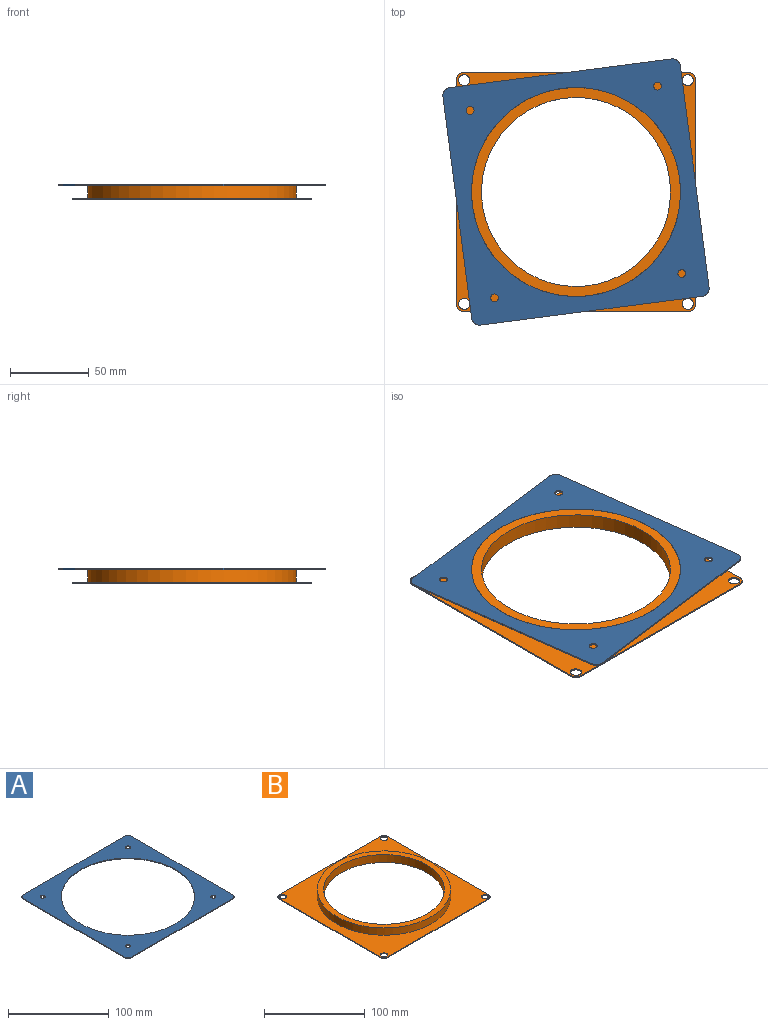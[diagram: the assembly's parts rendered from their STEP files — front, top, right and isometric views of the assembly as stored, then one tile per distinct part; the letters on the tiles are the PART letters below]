
ASSEMBLY  parts=2 mates=1
PART A: 15 faces, bbox 152x152x0.8 mm
  f0: cylinder r=5mm len=5mm, axis (0,0,1), area 6.3mm2, adj f1,f12,f13,f14
  f1: plane 142x0.8mm, normal (0,-1,0), area 113.6mm2, adj f0,f2,f13,f14
  f2: cylinder r=5mm len=5mm, axis (0,0,1), area 6.3mm2, adj f1,f3,f13,f14
  f3: plane 142x0.8mm, normal (1,0,0), area 113.6mm2, adj f2,f4,f13,f14
  f4: cylinder r=5mm len=5mm, axis (0,0,1), area 6.3mm2, adj f3,f5,f13,f14
  f5: plane 142x0.8mm, normal (0,1,0), area 113.6mm2, adj f4,f6,f13,f14
  f6: cylinder r=5mm len=5mm, axis (0,0,1), area 6.3mm2, adj f5,f12,f13,f14
  f7: cylinder r=2.5mm len=5mm, axis (0,0,1), area 12.6mm2, adj f13,f14
  f8: cylinder r=2.5mm len=5mm, axis (0,0,1), area 12.6mm2, adj f13,f14
  f9: cylinder r=2.5mm len=5mm, axis (0,0,1), area 12.6mm2, adj f13,f14
  f10: cylinder r=2.5mm len=5mm, axis (0,0,1), area 12.6mm2, adj f13,f14
  f11: cylinder r=66.35mm len=132.7mm, axis (0,0,1), area 333.5mm2, adj f13,f14
  f12: plane 142x0.8mm, normal (-1,0,0), area 113.6mm2, adj f0,f6,f13,f14
  f13: plane 152x152mm, normal (0,0,-1), area 9173.7mm2, adj f0,f1,f2,f3,f4,f5,f6,f7
  f14: plane 152x152mm, normal (0,0,1), area 9173.7mm2, adj f0,f1,f2,f3,f4,f5,f6,f7
PART B: 17 faces, bbox 152x152x9.6 mm
  f0: plane 142x0.8mm, normal (0,-1,0), area 113.6mm2, adj f1,f12,f13,f14
  f1: cylinder r=5mm len=5mm, axis (0,0,-1), area 6.3mm2, adj f0,f2,f13,f14
  f2: plane 142x0.8mm, normal (1,0,0), area 113.6mm2, adj f1,f3,f13,f14
  f3: cylinder r=5mm len=5mm, axis (0,0,-1), area 6.3mm2, adj f2,f4,f13,f14
  f4: plane 142x0.8mm, normal (0,1,0), area 113.6mm2, adj f3,f5,f13,f14
  f5: cylinder r=5mm len=5mm, axis (0,0,-1), area 6.3mm2, adj f4,f6,f13,f14
  f6: plane 142x0.8mm, normal (-1,0,0), area 113.6mm2, adj f5,f12,f13,f14
  f7: cylinder r=60mm len=120mm, axis (0,0,-1), area 3619.1mm2, adj f14,f16
  f8: cylinder r=3.5mm len=7mm, axis (0,0,-1), area 17.6mm2, adj f13,f14
  f9: cylinder r=3.5mm len=7mm, axis (0,0,-1), area 17.6mm2, adj f13,f14
  f10: cylinder r=3.5mm len=7mm, axis (0,0,-1), area 17.6mm2, adj f13,f14
  f11: cylinder r=3.5mm len=7mm, axis (0,0,-1), area 17.6mm2, adj f13,f14
  f12: cylinder r=5mm len=5mm, axis (0,0,-1), area 6.3mm2, adj f0,f6,f13,f14
  f13: plane 152x152mm, normal (0,0,1), area 9098.3mm2, adj f0,f1,f2,f3,f4,f5,f6,f8
  f14: plane 152x152mm, normal (0,0,-1), area 11618.9mm2, adj f0,f1,f2,f3,f4,f5,f6,f7
  f15: cylinder r=66.35mm len=132.7mm, axis (0,0,-1), area 3668.6mm2, adj f13,f16
  f16: plane 132.7x132.7mm, normal (0,0,1), area 2520.6mm2, adj f7,f15
PLACE A rot(axis=(0,0,-1),172.6deg) t=(0,0,0)mm
PLACE B at identity
MATE revolute A.f11 <-> B.f7  axis (0,0,1) through (0,0,9.6)mm
